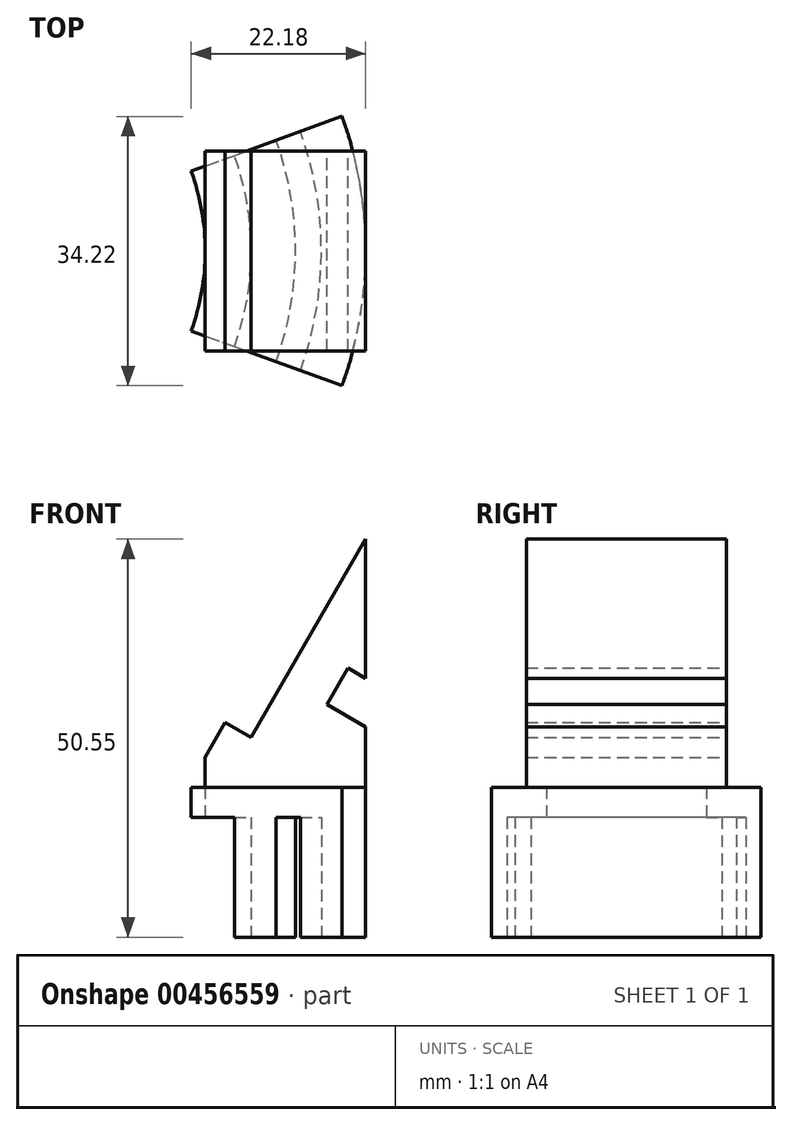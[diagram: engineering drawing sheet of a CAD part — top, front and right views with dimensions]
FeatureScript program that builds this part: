
annotation { "Feature Type Name" : "Feature", "Feature Type Description" : "" }
export const myFeature = defineFeature(function(context is Context, id is Id, definition is map)
    precondition{}
    {
        {
            var Q0;
            Q0=qCreatedBy(makeId("Front.planeOp"),FACE);
            var sketch = newSketch(context, id + "F0", { "sketchPlane" : qUnion([Q0])});
            skLineSegment(sketch, "E0", {"start": v(0, 0) * mm, "end": v(14.55, 25.2) * mm});
            skLineSegment(sketch, "E1", {"start": v(0, 0) * mm, "end": v(-3.3, 1.9) * mm});
            skLineSegment(sketch, "E2", {"start": v(-3.3, 1.9) * mm, "end": v(-5.84, -2.5) * mm});
            skLineSegment(sketch, "E3", {"start": v(-5.84, -10.11) * mm, "end": v(0, 0) * mm, "construction": true});
            skLineSegment(sketch, "E4", {"start": v(-5.84, -10.11) * mm, "end": v(0, -10.11) * mm});
            skLineSegment(sketch, "E5", {"start": v(14.55, 25.2) * mm, "end": v(14.55, -10.11) * mm});
            skLineSegment(sketch, "E6", {"start": v(0, -10.11) * mm, "end": v(0, -25.35) * mm});
            skLineSegment(sketch, "E7", {"start": v(0, -25.35) * mm, "end": v(5.64, -25.35) * mm});
            skLineSegment(sketch, "E8", {"start": v(5.64, -25.35) * mm, "end": v(5.64, -10.11) * mm});
            skLineSegment(sketch, "E9", {"start": v(8.91, -10.11) * mm, "end": v(8.91, -25.35) * mm});
            skLineSegment(sketch, "E10", {"start": v(8.91, -25.35) * mm, "end": v(14.55, -25.35) * mm});
            skLineSegment(sketch, "E11", {"start": v(14.55, -25.35) * mm, "end": v(14.55, -10.11) * mm});
            skLineSegment(sketch, "E12.trimOffspring", {"start": v(5.64, -10.11) * mm, "end": v(8.91, -10.11) * mm});
            skLineSegment(sketch, "E13", {"start": v(0, -25.35) * mm, "end": v(-35.49, -25.35) * mm, "construction": true});
            skLineSegment(sketch, "E14", {"start": v(-35.49, -25.35) * mm, "end": v(-35.49, 0) * mm, "construction": true});
            skLineSegment(sketch, "E15", {"start": v(-5.84, -2.5) * mm, "end": v(14.55, -2.5) * mm, "construction": true});
            skLineSegment(sketch, "E16", {"start": v(-5.84, -2.5) * mm, "end": v(-5.84, -10.11) * mm});
            skLineSegment(sketch, "E17", {"start": v(-5.84, -6.3) * mm, "end": v(14.55, -6.3) * mm});
            skPoint(sketch, "E17.startSnap0", {"position": v(-5.84, -6.3) * mm});
            skLineSegment(sketch, "E18", {"start": v(14.55, 7.54) * mm, "end": v(12.31, 8.84) * mm});
            skLineSegment(sketch, "E19", {"start": v(12.31, 8.84) * mm, "end": v(9.63, 4.2) * mm});
            skLineSegment(sketch, "E20", {"start": v(9.63, 4.2) * mm, "end": v(14.55, 1.35) * mm});
            skSolve(sketch);
        }
        {
            var Q0;
            {var subQ2=sQuery(id+"F0.wireOp",EDGE,"E4");Q0=makeQuery(id+"F0.imprint","IMPRINT",FACE,{"disambiguationData":[TD([[makeQuery(id+"F0.imprint","IMPRINT",EDGE,{"derivedFrom":subQ2}),1.0]])]});}
            var Q1;
            Q1=sQuery(id+"F0.wireOp",EDGE,"E14");
            revolve(context, id + "F1", {"entities" : qUnion([Q0]), "axis" : qUnion([Q1]), "revolveType" : RevolveType.SYMMETRIC, "angle" : 40 * degree});
        }
        {
            var Q0;
            {var subQ1=sQuery(id+"F0.wireOp",EDGE,"E0");Q0=makeQuery(id+"F0.imprint","IMPRINT",FACE,{"disambiguationData":[TD([[makeQuery(id+"F0.imprint","IMPRINT",EDGE,{"derivedFrom":subQ1}),-1.0]])]});}
            extrude(context, id + "F2", {"entities" : qUnion([Q0]), "operationType" : NewBodyOperationType.ADD, "depth" : 12.7 * mm});
        }
        {
            var Q0;
            {var subQ1=sQuery(id+"F0.wireOp",EDGE,"E0");Q0=makeQuery(id+"F0.imprint","IMPRINT",FACE,{"disambiguationData":[TD([[makeQuery(id+"F0.imprint","IMPRINT",EDGE,{"derivedFrom":subQ1}),-1.0]])]});}
            extrude(context, id + "F3", {"entities" : qUnion([Q0]), "operationType" : NewBodyOperationType.ADD, "oppositeDirection" : true, "depth" : 12.7 * mm});
        }
    });
